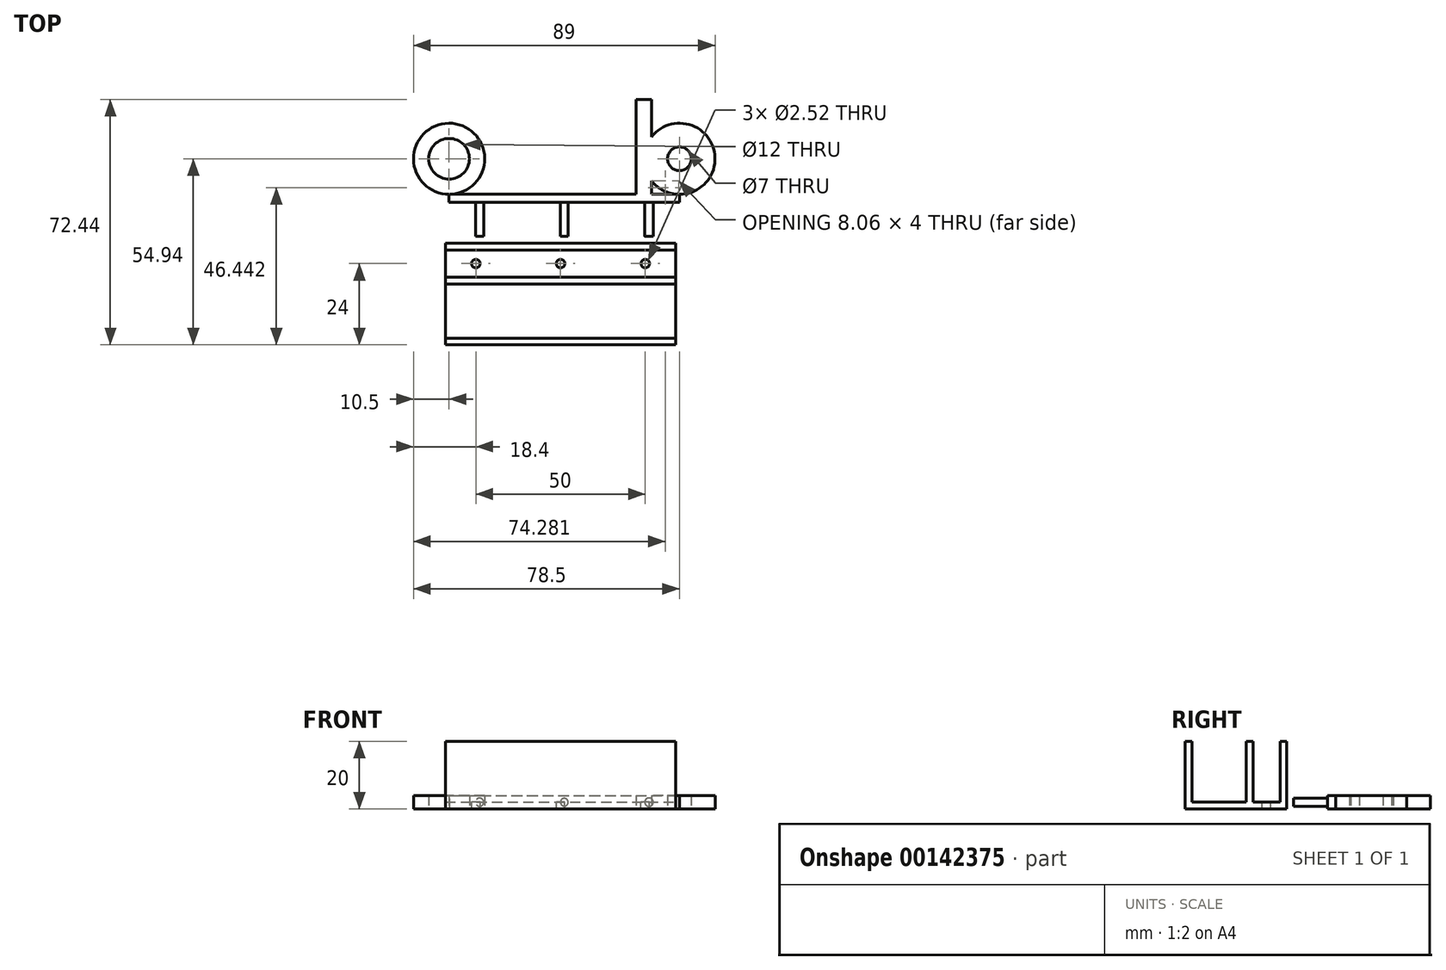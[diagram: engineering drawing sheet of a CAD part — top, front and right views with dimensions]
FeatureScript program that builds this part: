
annotation { "Feature Type Name" : "Feature", "Feature Type Description" : "" }
export const myFeature = defineFeature(function(context is Context, id is Id, definition is map)
    precondition{}
    {
        {
            var Q0;
            Q0=qCreatedBy(makeId("Top.planeOp"),FACE);
            var sketch = newSketch(context, id + "F0", { "sketchPlane" : qUnion([Q0])});
            skCircle(sketch, "E0", {"center": v(0, 0) * mm, "radius": 10.5 * mm});
            skCircle(sketch, "E1", {"center": v(37.5, 0) * mm, "radius": 7 * mm});
            skCircle(sketch, "E2", {"center": v(68, 0) * mm, "radius": 3.5 * mm});
            skSolve(sketch);
        }
        {
            var Q0;
            Q0=qCreatedBy(makeId("Top.planeOp"),FACE);
            var sketch = newSketch(context, id + "F1", { "sketchPlane" : qUnion([Q0])});
            skCircle(sketch, "E3.0", {"center": v(0, 0) * mm, "radius": 10.5 * mm});
            skCircle(sketch, "E3.1", {"center": v(37.5, 0) * mm, "radius": 7 * mm});
            skCircle(sketch, "E3.2", {"center": v(68, 0) * mm, "radius": 3.5 * mm});
            skLineSegment(sketch, "E4", {"start": v(10.5, 0) * mm, "end": v(10.5, -10.5) * mm});
            skLineSegment(sketch, "E5", {"start": v(10.5, -10.5) * mm, "end": v(6, -10.5) * mm});
            skLineSegment(sketch, "E6", {"start": v(6, -10.5) * mm, "end": v(6, -8.62) * mm});
            skCircle(sketch, "E7", {"center": v(0, 0) * mm, "radius": 6 * mm});
            skLineSegment(sketch, "E8", {"start": v(42.45, 4.95) * mm, "end": v(45.63, 8.13) * mm});
            skLineSegment(sketch, "E9", {"start": v(32.75, -5.14) * mm, "end": v(32.75, -10.5) * mm});
            skLineSegment(sketch, "E10", {"start": v(32.75, -10.5) * mm, "end": v(28.25, -10.5) * mm});
            skLineSegment(sketch, "E11", {"start": v(0, -10.5) * mm, "end": v(85.92, -10.5) * mm, "construction": true});
            skLineSegment(sketch, "E12", {"start": v(30.5, 0) * mm, "end": v(30.5, -10.5) * mm, "construction": true});
            skLineSegment(sketch, "E13", {"start": v(37.5, 7) * mm, "end": v(44.5, 7) * mm, "construction": true});
            skLineSegment(sketch, "E14", {"start": v(44.5, 7) * mm, "end": v(44.5, 0) * mm, "construction": true});
            skLineSegment(sketch, "E15", {"start": v(37.5, 7) * mm, "end": v(24.33, 7) * mm, "construction": true});
            skLineSegment(sketch, "E16", {"start": v(37.5, 7) * mm, "end": v(37.5, 11.82) * mm, "construction": true});
            skLineSegment(sketch, "E17", {"start": v(28.25, -10.5) * mm, "end": v(28.25, 7) * mm, "construction": true});
            skFitSpline(sketch, "E18", {"points": [v(28.25, -10.5) * mm, v(28.25, 7) * mm, v(37.5, 11.82) * mm, v(45.63, 8.13) * mm], "startDerivative": vector(-9.02, 49.68) * mm, "endDerivative": vector(26.27, -18.51) * mm});
            skLineSegment(sketch, "E19", {"start": v(55.25, -10.5) * mm, "end": v(55.25, 17.5) * mm});
            skLineSegment(sketch, "E20", {"start": v(55.25, 17.5) * mm, "end": v(59.75, 17.5) * mm});
            skLineSegment(sketch, "E21", {"start": v(59.75, 17.5) * mm, "end": v(59.75, -10.5) * mm});
            skLineSegment(sketch, "E22", {"start": v(59.75, -10.5) * mm, "end": v(55.25, -10.5) * mm});
            skCircle(sketch, "E23", {"center": v(68, 0) * mm, "radius": 10.5 * mm});
            skLineSegment(sketch, "E24", {"start": v(57.5, -10.5) * mm, "end": v(57.5, 17.5) * mm, "construction": true});
            skSolve(sketch);
        }
        {
            var Q0;
            Q0 = qSketchRegion(id + "F1", true);
            extrude(context, id + "F2", {"entities" : qUnion([Q0]), "depth" : 4 * mm});
        }
        {
            var Q0;
            Q0=makeQuery(id+"F0.imprint","IMPRINT",FACE,{"disambiguationData":[TD([[makeQuery(id+"F0.imprint","IMPRINT",EDGE,{"derivedFrom":sQuery(id+"F0.wireOp",EDGE,"E1")}),1.0]])]});
            extrude(context, id + "F3", {"entities" : qUnion([Q0]), "operationType" : NewBodyOperationType.REMOVE, "depth" : 25 * mm});
        }
        {
            var Q0;
            Q0=qCreatedBy(makeId("Top.planeOp"),FACE);
            var sketch = newSketch(context, id + "F4", { "sketchPlane" : qUnion([Q0])});
            skLineSegment(sketch, "E25.0", {"start": v(10.5, -10.5) * mm, "end": v(6, -10.5) * mm});
            skArc(sketch, "E25.1", {"start": v(10.5, 0) * mm, "mid": v(-9.3, 4.86) * mm, "end": v(6, -8.62) * mm});
            skLineSegment(sketch, "E25.2", {"start": v(32.75, -10.5) * mm, "end": v(28.25, -10.5) * mm});
            skLineSegment(sketch, "E25.3", {"start": v(59.75, -10.5) * mm, "end": v(55.25, -10.5) * mm});
            skArc(sketch, "E25.4", {"start": v(59.75, -6.5) * mm, "mid": v(78.5, 0) * mm, "end": v(59.75, 6.5) * mm});
            skLineSegment(sketch, "E26.bottom", {"start": v(0, -10.5) * mm, "end": v(68, -10.5) * mm});
            skLineSegment(sketch, "E26.top", {"start": v(0, -12.9) * mm, "end": v(68, -12.9) * mm});
            skLineSegment(sketch, "E26.left", {"start": v(0, -10.5) * mm, "end": v(0, -12.9) * mm});
            skLineSegment(sketch, "E26.right", {"start": v(68, -10.5) * mm, "end": v(68, -12.9) * mm});
            skLineSegment(sketch, "E27.top", {"start": v(0, -10.49) * mm, "end": v(68, -10.49) * mm});
            skLineSegment(sketch, "E27.left", {"start": v(0, -10.5) * mm, "end": v(0, -10.49) * mm});
            skLineSegment(sketch, "E27.right", {"start": v(68, -10.5) * mm, "end": v(68, -10.49) * mm});
            skSolve(sketch);
        }
        {
            var Q0;
            Q0=makeQuery(id+"F4.imprint","IMPRINT",FACE,{"disambiguationData":[TD([[makeQuery(id+"F4.imprint","IMPRINT",EDGE,{"derivedFrom":sQuery(id+"F4.wireOp",EDGE,"E26.top")}),1.0]])]});
            var Q1;
            {var subQ0=sQuery(id+"F4.wireOp",EDGE,"E26.bottom");var subQ3=makeQuery(id+"F4.imprint","IMPRINT",VERTEX,{"disambiguationData":[OD(0.0)],"derivedFrom":subQ0});Q1=makeQuery(id+"F4.imprint","IMPRINT",FACE,{"disambiguationData":[TD([[makeQuery(id+"F4.imprint","IMPRINT",EDGE,{"disambiguationData":[TD([[subQ3,-1.0]])],"derivedFrom":subQ0}),1.0]])]});}
            extrude(context, id + "F5", {"entities" : qUnion([Q0, Q1]), "depth" : 4 * mm});
        }
        {
            var Q0;
            Q0=makeQuery(id+"F5.opExtrude","SWEPT_FACE",FACE,{"disambiguationData":[OSD([sQuery(id+"F4.wireOp",EDGE,"E26.top")])]});
            var sketch = newSketch(context, id + "F6", { "sketchPlane" : qUnion([Q0])});
            skCircle(sketch, "E28", {"center": v(9, 2) * mm, "radius": 1.21 * mm});
            skLineSegment(sketch, "E29", {"start": v(0, 2) * mm, "end": v(68, 2) * mm, "construction": true});
            skCircle(sketch, "E30", {"center": v(34, 2) * mm, "radius": 1.14 * mm});
            skCircle(sketch, "E31", {"center": v(59, 2) * mm, "radius": 1.25 * mm});
            skLineSegment(sketch, "E32", {"start": v(9, 2) * mm, "end": v(0, 2) * mm, "construction": true});
            skLineSegment(sketch, "E33", {"start": v(59, 2) * mm, "end": v(68, 2) * mm, "construction": true});
            skSolve(sketch);
        }
        {
            var Q0;
            Q0 = qSketchRegion(id + "F6", true);
            extrude(context, id + "F7", {"entities" : qUnion([Q0]), "operationType" : NewBodyOperationType.ADD, "depth" : 10 * mm});
        }
        {
            var Q0;
            Q0=makeQuery(id+"F2.opExtrude","SWEPT_BODY",BODY,{"disambiguationData":[OSD([sQuery(id+"F1.wireOp",EDGE,"E3.0"),sQuery(id+"F1.wireOp",EDGE,"E4"),sQuery(id+"F1.wireOp",EDGE,"E5"),sQuery(id+"F1.wireOp",EDGE,"E6"),sQuery(id+"F1.wireOp",EDGE,"E7")])]});
            var Q1;
            Q1=makeQuery(id+"F2.opExtrude","SWEPT_BODY",BODY,{"disambiguationData":[OSD([sQuery(id+"F1.wireOp",EDGE,"E3.1"),sQuery(id+"F1.wireOp",EDGE,"E8"),sQuery(id+"F1.wireOp",EDGE,"E9"),sQuery(id+"F1.wireOp",EDGE,"E10"),sQuery(id+"F1.wireOp",EDGE,"E18")])]});
            var Q2;
            Q2=makeQuery(id+"F2.opExtrude","SWEPT_BODY",BODY,{"disambiguationData":[OSD([sQuery(id+"F1.wireOp",EDGE,"E3.2"),sQuery(id+"F1.wireOp",EDGE,"E19"),sQuery(id+"F1.wireOp",EDGE,"E20"),sQuery(id+"F1.wireOp",EDGE,"E21"),sQuery(id+"F1.wireOp",EDGE,"E22"),sQuery(id+"F1.wireOp",EDGE,"E23")])]});
            var Q3;
            Q3=makeQuery(id+"F5.opExtrude","SWEPT_BODY",BODY,{"disambiguationData":[OSD([sQuery(id+"F4.wireOp",EDGE,"E25.1"),sQuery(id+"F4.wireOp",EDGE,"E25.4"),sQuery(id+"F4.wireOp",EDGE,"E26.top"),sQuery(id+"F4.wireOp",EDGE,"E26.left"),sQuery(id+"F4.wireOp",EDGE,"E26.right"),sQuery(id+"F4.wireOp",EDGE,"E27.top")])]});
            booleanBodies(context, id + "F8", {"operationType" : BooleanOperationType.UNION, "tools" : qUnion([Q0, Q1, Q2, Q3])});
        }
        {
            var Q0;
            Q0=qCreatedBy(makeId("Top.planeOp"),FACE);
            var sketch = newSketch(context, id + "F9", { "sketchPlane" : qUnion([Q0])});
            skLineSegment(sketch, "E34.bottom", {"start": v(-1.1, -24.94) * mm, "end": v(66.9, -24.94) * mm});
            skLineSegment(sketch, "E34.top", {"start": v(-1.1, -54.94) * mm, "end": v(66.9, -54.94) * mm});
            skLineSegment(sketch, "E34.left", {"start": v(-1.1, -24.94) * mm, "end": v(-1.1, -54.94) * mm});
            skLineSegment(sketch, "E34.right", {"start": v(66.9, -24.94) * mm, "end": v(66.9, -54.94) * mm});
            skLineSegment(sketch, "E35.0", {"start": v(0, -12.9) * mm, "end": v(68, -12.9) * mm});
            skSolve(sketch);
        }
        {
            var Q0;
            Q0=makeQuery(id+"F9.imprint","IMPRINT",FACE,{"disambiguationData":[TD([[makeQuery(id+"F9.imprint","IMPRINT",EDGE,{"derivedFrom":sQuery(id+"F9.wireOp",EDGE,"E34.bottom")}),-1.0]])]});
            extrude(context, id + "F10", {"entities" : qUnion([Q0]), "depth" : 20 * mm});
        }
        {
            var Q0;
            Q0=makeQuery(id+"F10.opExtrude","CAP_FACE",FACE,{"disambiguationData":[OSD([sQuery(id+"F9.wireOp",EDGE,"E34.bottom"),sQuery(id+"F9.wireOp",EDGE,"E34.top"),sQuery(id+"F9.wireOp",EDGE,"E34.left"),sQuery(id+"F9.wireOp",EDGE,"E34.right")])],"isStart":false});
            var sketch = newSketch(context, id + "F11", { "sketchPlane" : qUnion([Q0])});
            skLineSegment(sketch, "E36.bottom", {"start": v(-1.1, -52.94) * mm, "end": v(66.9, -52.94) * mm});
            skLineSegment(sketch, "E36.top", {"start": v(-1.1, -36.94) * mm, "end": v(66.9, -36.94) * mm});
            skLineSegment(sketch, "E36.left", {"start": v(-1.1, -52.94) * mm, "end": v(-1.1, -36.94) * mm});
            skLineSegment(sketch, "E36.right", {"start": v(66.9, -52.94) * mm, "end": v(66.9, -36.94) * mm});
            skLineSegment(sketch, "E37", {"start": v(24.64, -52.94) * mm, "end": v(24.64, -54.94) * mm, "construction": true});
            skLineSegment(sketch, "E38", {"start": v(23.82, -36.94) * mm, "end": v(23.82, -34.94) * mm, "construction": true});
            skLineSegment(sketch, "E39.bottom", {"start": v(-1.1, -34.94) * mm, "end": v(66.9, -34.94) * mm});
            skLineSegment(sketch, "E39.top", {"start": v(-1.1, -26.94) * mm, "end": v(66.9, -26.94) * mm});
            skLineSegment(sketch, "E39.left", {"start": v(-1.1, -34.94) * mm, "end": v(-1.1, -26.94) * mm});
            skLineSegment(sketch, "E39.right", {"start": v(66.9, -34.94) * mm, "end": v(66.9, -26.94) * mm});
            skLineSegment(sketch, "E40", {"start": v(4.68, -26.94) * mm, "end": v(4.68, -24.94) * mm, "construction": true});
            skSolve(sketch);
        }
        {
            var Q0;
            Q0=makeQuery(id+"F11.imprint","IMPRINT",FACE,{"disambiguationData":[TD([[makeQuery(id+"F11.imprint","IMPRINT",EDGE,{"derivedFrom":sQuery(id+"F11.wireOp",EDGE,"E39.bottom")}),1.0]])]});
            var Q1;
            Q1=makeQuery(id+"F11.imprint","IMPRINT",FACE,{"disambiguationData":[TD([[makeQuery(id+"F11.imprint","IMPRINT",EDGE,{"derivedFrom":sQuery(id+"F11.wireOp",EDGE,"E36.bottom")}),1.0]])]});
            extrude(context, id + "F12", {"entities" : qUnion([Q0, Q1]), "operationType" : NewBodyOperationType.REMOVE, "oppositeDirection" : true, "depth" : 18 * mm});
        }
        {
            var Q0;
            Q0=makeQuery(id+"F12.boolean.opBoolean","COPY",FACE,{"derivedFrom":makeQuery(id+"F12.opExtrude","CAP_FACE",FACE,{"disambiguationData":[OSD([sQuery(id+"F11.wireOp",EDGE,"E39.bottom"),sQuery(id+"F11.wireOp",EDGE,"E39.top"),sQuery(id+"F11.wireOp",EDGE,"E39.left"),sQuery(id+"F11.wireOp",EDGE,"E39.right")])],"isStart":false})});
            var sketch = newSketch(context, id + "F13", { "sketchPlane" : qUnion([Q0])});
            skLineSegment(sketch, "E41", {"start": v(-1.1, -30.94) * mm, "end": v(7.9, -30.94) * mm, "construction": true});
            skLineSegment(sketch, "E42", {"start": v(66.9, -30.94) * mm, "end": v(57.9, -30.94) * mm, "construction": true});
            skPoint(sketch, "E42.endSnap0", {"position": v(66.9, -30.94) * mm});
            skLineSegment(sketch, "E43", {"start": v(32.9, -26.94) * mm, "end": v(32.9, -30.94) * mm, "construction": true});
            skLineSegment(sketch, "E44", {"start": v(32.9, -30.94) * mm, "end": v(32.9, -34.94) * mm, "construction": true});
            skCircle(sketch, "E45", {"center": v(7.9, -30.94) * mm, "radius": 1.26 * mm});
            skCircle(sketch, "E46", {"center": v(32.9, -30.94) * mm, "radius": 1.26 * mm});
            skCircle(sketch, "E47", {"center": v(57.9, -30.94) * mm, "radius": 1.26 * mm});
            skSolve(sketch);
        }
        {
            var Q0;
            Q0=makeQuery(id+"F13.imprint","IMPRINT",FACE,{"disambiguationData":[TD([[makeQuery(id+"F13.imprint","IMPRINT",EDGE,{"derivedFrom":sQuery(id+"F13.wireOp",EDGE,"E45")}),1.0]])]});
            var Q1;
            Q1=makeQuery(id+"F13.imprint","IMPRINT",FACE,{"disambiguationData":[TD([[makeQuery(id+"F13.imprint","IMPRINT",EDGE,{"derivedFrom":sQuery(id+"F13.wireOp",EDGE,"E46")}),1.0]])]});
            var Q2;
            Q2=makeQuery(id+"F13.imprint","IMPRINT",FACE,{"disambiguationData":[TD([[makeQuery(id+"F13.imprint","IMPRINT",EDGE,{"derivedFrom":sQuery(id+"F13.wireOp",EDGE,"E47")}),1.0]])]});
            var Q3;
            Q3=sQuery(id+"F13.wireOp",EDGE,"E45");
            var Q4;
            Q4=sQuery(id+"F13.wireOp",EDGE,"E46");
            var Q5;
            Q5=sQuery(id+"F13.wireOp",EDGE,"E47");
            extrude(context, id + "F14", {"entities" : qUnion([Q0, Q1, Q2]), "operationType" : NewBodyOperationType.REMOVE, "surfaceEntities" : qUnion([Q3, Q4, Q5]), "oppositeDirection" : true, "depth" : 25 * mm});
        }
    });
